# Revit family: Convection_Heater-QMark-ASLC
name_source: partatom
category: Mechanical Equipment
revit_build: Autodesk Revit 2016 (Build: 20150220_1215(x64)
units: mm (PartAtom-declared; Revit-internal decimal feet)

## family parameters
Cut with Voids When Loaded = No
Host = Face
OmniClass Number = 23.75.70.17.14
OmniClass Title = Convectors
Part Type = Normal
Room Calculation Point = No
Round Connector Dimension = Use Diameter
Shared = No

## types (10) — shared parameters
Amps = 1 A
Apparent Load = 0 VA
Casing = Metal - Berko - Paint - Aluminum
Default Elevation = 0' - 3"
Description = Architectural Electric Convectors
Frequency = 60 Hz
Height = 0' - 6"
Manufacturer = Marley Engineered Products
Minimum Distance From Drapes = 0' - 2"
Minimum Distance From Window Sill = 1' - 0"
Model = ASLC
Number of Poles = 1
Phase = 2
Power Factor = 1
Product Documentation Link = https://www.marleymep.com
Product Name = Slimline Aluminum Convector - ASLC Series
Product Page URL = https://www.marleymep.com
URL = http://www.marleymep.com
Voltage = 240 V
Width = 0' - 3 5/8"

## per-type parameters (varying)
| type | Length | Length Constraint | Watts |
| ASLC01 | 2' - 0" | 2' - 4" | 250 W |
| ASLC02 | 2' - 4" | 2' - 4" | 233 W |
| ASLC03 | 3' - 0" | 3' - 0" | 300 W |
| ASLC04 | 4' - 0" | 4' - 0" | 400 W |
| ASLC05 | 5' - 0" | 5' - 0" | 500 W |
| ASLC06 | 6' - 0" | 6' - 0" | 600 W |
| ASLC07 | 7' - 0" | 7' - 0" | 700 W |
| ASLC08 | 8' - 0" | 8' - 0" | 800 W |
| ASLC09 | 9' - 0" | 9' - 0" | 900 W |
| ASLC10 | 10' - 0" | 10' - 0" | 1000 W |

## geometry (parser evidence)
native form markers: Blend x1, Sweep x1
no freeform markers — native parametric forms only
